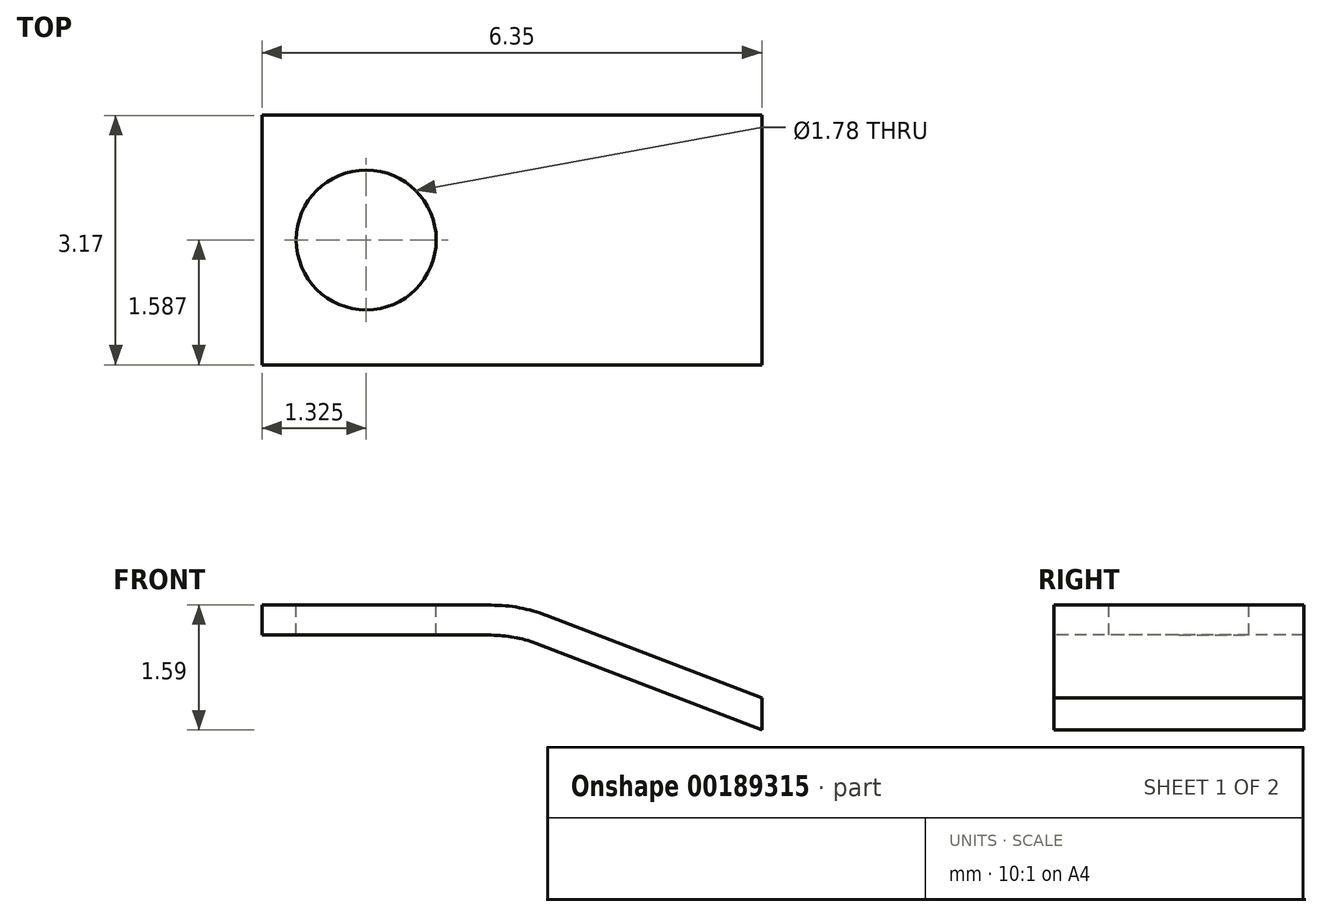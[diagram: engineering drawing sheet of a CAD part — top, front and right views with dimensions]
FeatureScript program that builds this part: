
annotation { "Feature Type Name" : "Feature", "Feature Type Description" : "" }
export const myFeature = defineFeature(function(context is Context, id is Id, definition is map)
    precondition{}
    {
        {
            var Q0;
            Q0=qCreatedBy(makeId("Front.planeOp"),FACE);
            var sketch = newSketch(context, id + "F0", { "sketchPlane" : qUnion([Q0])});
            skLineSegment(sketch, "E0.left", {"start": v(0, 1.2) * mm, "end": v(0, 1.59) * mm});
            skLineSegment(sketch, "E0.right", {"start": v(6.35, 0) * mm, "end": v(6.35, 0.4) * mm});
            skLineSegment(sketch, "E1", {"start": v(0, 1.2) * mm, "end": v(2.91, 1.2) * mm});
            skLineSegment(sketch, "E2", {"start": v(6.35, 0) * mm, "end": v(3.48, 1.1) * mm});
            skPoint(sketch, "E3.visualSharp", {"position": v(3.2, 1.2) * mm});
            skArc(sketch, "E3.filletArc", {"start": v(3.48, 1.1) * mm, "mid": v(3.2, 1.18) * mm, "end": v(2.91, 1.2) * mm});
            skLineSegment(sketch, "E4.0", {"start": v(6.35, 0.4) * mm, "end": v(3.62, 1.46) * mm});
            skArc(sketch, "E4.1", {"start": v(3.62, 1.46) * mm, "mid": v(3.27, 1.55) * mm, "end": v(2.91, 1.59) * mm});
            skLineSegment(sketch, "E4.2", {"start": v(0, 1.59) * mm, "end": v(2.91, 1.59) * mm});
            skSolve(sketch);
        }
        {
            var Q0;
            Q0 = qSketchRegion(id + "F0", true);
            extrude(context, id + "F1", {"entities" : qUnion([Q0]), "oppositeDirection" : true, "depth" : 3.17 * mm});
        }
        {
            var Q0;
            Q0=makeQuery(id+"F1.opExtrude","SWEPT_FACE",FACE,{"disambiguationData":[OSD([sQuery(id+"F0.wireOp",EDGE,"E4.2")])]});
            var sketch = newSketch(context, id + "F2", { "sketchPlane" : qUnion([Q0])});
            skPoint(sketch, "E5", {"position": v(1.33, 1.59) * mm});
            skSolve(sketch);
        }
        {
            var Q0;
            Q0=sQuery(id+"F2.wireOp",VERTEX,"E5");
            var Q1;
            Q1=makeQuery(id+"F1.opExtrude","SWEPT_BODY",BODY,{"disambiguationData":[OSD([sQuery(id+"F0.wireOp",EDGE,"E0.left"),sQuery(id+"F0.wireOp",EDGE,"E0.right"),sQuery(id+"F0.wireOp",EDGE,"E1"),sQuery(id+"F0.wireOp",EDGE,"E2"),sQuery(id+"F0.wireOp",EDGE,"E3.filletArc"),sQuery(id+"F0.wireOp",EDGE,"E4.0"),sQuery(id+"F0.wireOp",EDGE,"E4.1"),sQuery(id+"F0.wireOp",EDGE,"E4.2")])]});
            hole(context, id + "F3", {"style" : HoleStyle.SIMPLE, "endStyle" : HoleEndStyle.THROUGH, "standardTappedOrClearance" : lookupTablePath({ "standard" : "ANSI", "fit" : "Normal (ASME)", "size" : "#0", "type" : "Clearance" }), "standardBlindInLast" : lookupTablePath({ "fit" : "Free", "standard" : "ANSI", "size" : "#0", "type" : "Clearance" }), "holeDiameter" : 1.78 * mm, "locations" : qUnion([Q0]), "scope" : qUnion([Q1]), "isTappedThrough" : true});
        }
    });
